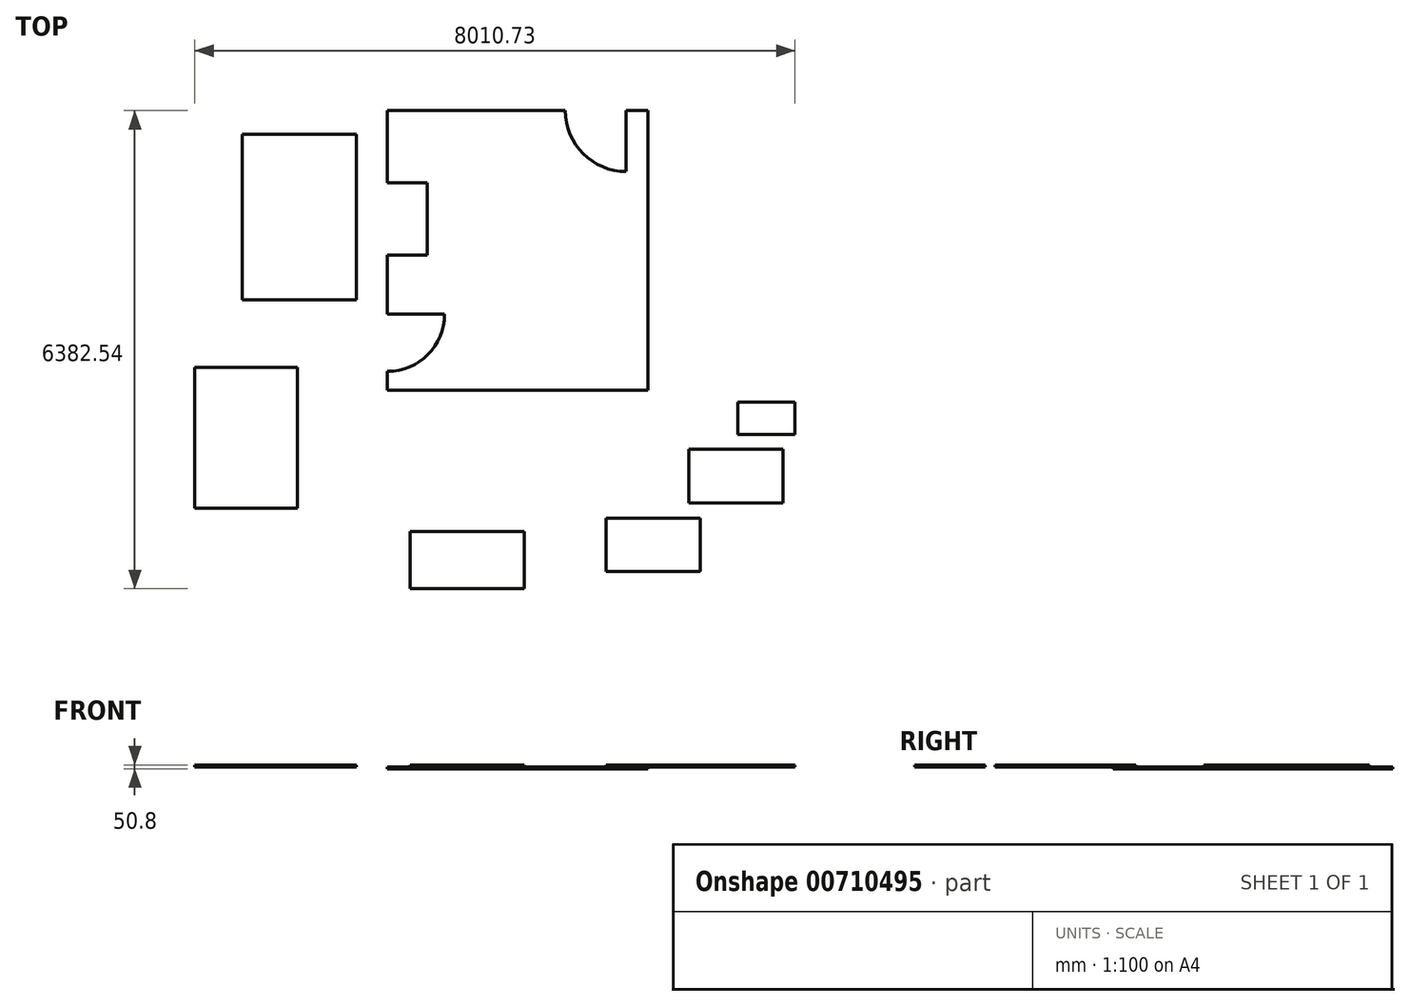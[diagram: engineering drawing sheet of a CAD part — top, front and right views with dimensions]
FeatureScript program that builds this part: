
annotation { "Feature Type Name" : "Feature", "Feature Type Description" : "" }
export const myFeature = defineFeature(function(context is Context, id is Id, definition is map)
    precondition{}
    {
        {
            var Q0;
            Q0=qCreatedBy(makeId("Top.planeOp"),FACE);
            var sketch = newSketch(context, id + "F0", { "sketchPlane" : qUnion([Q0])});
            skLineSegment(sketch, "E0", {"start": v(-1733.33, 2522.98) * mm, "end": v(641.57, 2522.98) * mm});
            skLineSegment(sketch, "E1", {"start": v(1746.47, 2522.98) * mm, "end": v(1746.47, -1210.82) * mm});
            skLineSegment(sketch, "E2", {"start": v(1746.47, -1210.82) * mm, "end": v(-1733.33, -1210.82) * mm});
            skLineSegment(sketch, "E3", {"start": v(-1733.33, -1210.82) * mm, "end": v(-1733.33, -956.82) * mm});
            skLineSegment(sketch, "E4", {"start": v(-1733.33, 592.58) * mm, "end": v(-1199.93, 592.58) * mm});
            skLineSegment(sketch, "E5", {"start": v(-1199.93, 592.58) * mm, "end": v(-1199.93, 1557.78) * mm});
            skLineSegment(sketch, "E6", {"start": v(-1199.93, 1557.78) * mm, "end": v(-1733.33, 1557.78) * mm});
            skLineSegment(sketch, "E7", {"start": v(-1733.33, 1557.78) * mm, "end": v(-1733.33, 2522.98) * mm});
            skArc(sketch, "E8", {"start": v(-1733.33, -956.82) * mm, "mid": v(-1194.52, -733.64) * mm, "end": v(-971.33, -194.82) * mm});
            skLineSegment(sketch, "E9", {"start": v(-1733.33, -194.82) * mm, "end": v(-971.33, -194.82) * mm});
            skLineSegment(sketch, "E10.trimOffspring", {"start": v(-1733.33, -194.82) * mm, "end": v(-1733.33, 592.58) * mm});
            skArc(sketch, "E11", {"start": v(641.57, 2522.98) * mm, "mid": v(879.63, 1948.24) * mm, "end": v(1454.37, 1710.18) * mm});
            skLineSegment(sketch, "E12", {"start": v(1454.37, 2522.98) * mm, "end": v(1454.37, 1710.18) * mm});
            skLineSegment(sketch, "E13.trimOffspring", {"start": v(1454.37, 2522.98) * mm, "end": v(1746.47, 2522.98) * mm});
            skSolve(sketch);
        }
        {
            var Q0;
            Q0 = qSketchRegion(id + "F0", true);
            extrude(context, id + "F1", {"entities" : qUnion([Q0]), "depth" : 25.4 * mm, "offsetDistance" : 25.4 * mm});
        }
        {
            var Q0;
            Q0=makeQuery(id+"F1.opExtrude","CAP_FACE",FACE,{"disambiguationData":[OSD([sQuery(id+"F0.wireOp",EDGE,"E0"),sQuery(id+"F0.wireOp",EDGE,"E1"),sQuery(id+"F0.wireOp",EDGE,"E2"),sQuery(id+"F0.wireOp",EDGE,"E3"),sQuery(id+"F0.wireOp",EDGE,"E4"),sQuery(id+"F0.wireOp",EDGE,"E5"),sQuery(id+"F0.wireOp",EDGE,"E6"),sQuery(id+"F0.wireOp",EDGE,"E7")])],"isStart":false});
            var sketch = newSketch(context, id + "F2", { "sketchPlane" : qUnion([Q0])});
            skLineSegment(sketch, "E14.bottom", {"start": v(-3670.25, 2209.8) * mm, "end": v(-2146.25, 2209.8) * mm});
            skLineSegment(sketch, "E14.top", {"start": v(-3670.25, 0) * mm, "end": v(-2146.25, 0) * mm});
            skLineSegment(sketch, "E14.left", {"start": v(-3670.25, 2209.8) * mm, "end": v(-3670.25, 0) * mm});
            skLineSegment(sketch, "E14.right", {"start": v(-2146.25, 2209.8) * mm, "end": v(-2146.25, 0) * mm});
            skSolve(sketch);
        }
        {
            var Q0;
            Q0=makeQuery(id+"F2.imprint","IMPRINT",FACE,{"disambiguationData":[TD([[makeQuery(id+"F2.imprint","IMPRINT",EDGE,{"derivedFrom":sQuery(id+"F2.wireOp",EDGE,"E14.bottom")}),-1.0]])]});
            extrude(context, id + "F3", {"entities" : qUnion([Q0]), "depth" : 25.4 * mm, "offsetDistance" : 25.4 * mm});
        }
        {
            var Q0;
            Q0=makeQuery(id+"F1.opExtrude","CAP_FACE",FACE,{"disambiguationData":[OSD([sQuery(id+"F0.wireOp",EDGE,"E0"),sQuery(id+"F0.wireOp",EDGE,"E1"),sQuery(id+"F0.wireOp",EDGE,"E2"),sQuery(id+"F0.wireOp",EDGE,"E3"),sQuery(id+"F0.wireOp",EDGE,"E4"),sQuery(id+"F0.wireOp",EDGE,"E5"),sQuery(id+"F0.wireOp",EDGE,"E6"),sQuery(id+"F0.wireOp",EDGE,"E7")])],"isStart":false});
            var sketch = newSketch(context, id + "F4", { "sketchPlane" : qUnion([Q0])});
            skLineSegment(sketch, "E15.bottom", {"start": v(-4305.32, -903.13) * mm, "end": v(-2933.72, -903.13) * mm});
            skLineSegment(sketch, "E15.top", {"start": v(-4305.32, -2782.73) * mm, "end": v(-2933.72, -2782.73) * mm});
            skLineSegment(sketch, "E15.left", {"start": v(-4305.32, -903.13) * mm, "end": v(-4305.32, -2782.73) * mm});
            skLineSegment(sketch, "E15.right", {"start": v(-2933.72, -903.13) * mm, "end": v(-2933.72, -2782.73) * mm});
            skSolve(sketch);
        }
        {
            var Q0;
            Q0=makeQuery(id+"F4.imprint","IMPRINT",FACE,{"disambiguationData":[TD([[makeQuery(id+"F4.imprint","IMPRINT",EDGE,{"derivedFrom":sQuery(id+"F4.wireOp",EDGE,"E15.bottom")}),-1.0]])]});
            extrude(context, id + "F5", {"entities" : qUnion([Q0]), "depth" : 25.4 * mm, "offsetDistance" : 25.4 * mm});
        }
        {
            var Q0;
            Q0=makeQuery(id+"F1.opExtrude","CAP_FACE",FACE,{"disambiguationData":[OSD([sQuery(id+"F0.wireOp",EDGE,"E0"),sQuery(id+"F0.wireOp",EDGE,"E1"),sQuery(id+"F0.wireOp",EDGE,"E2"),sQuery(id+"F0.wireOp",EDGE,"E3"),sQuery(id+"F0.wireOp",EDGE,"E4"),sQuery(id+"F0.wireOp",EDGE,"E5"),sQuery(id+"F0.wireOp",EDGE,"E6"),sQuery(id+"F0.wireOp",EDGE,"E7")])],"isStart":false});
            var sketch = newSketch(context, id + "F6", { "sketchPlane" : qUnion([Q0])});
            skLineSegment(sketch, "E16.bottom", {"start": v(-1434.19, -3097.56) * mm, "end": v(89.81, -3097.56) * mm});
            skLineSegment(sketch, "E16.top", {"start": v(-1434.19, -3859.56) * mm, "end": v(89.81, -3859.56) * mm});
            skLineSegment(sketch, "E16.left", {"start": v(-1434.19, -3097.56) * mm, "end": v(-1434.19, -3859.56) * mm});
            skLineSegment(sketch, "E16.right", {"start": v(89.81, -3097.56) * mm, "end": v(89.81, -3859.56) * mm});
            skSolve(sketch);
        }
        {
            var Q0;
            Q0=makeQuery(id+"F6.imprint","IMPRINT",FACE,{"disambiguationData":[TD([[makeQuery(id+"F6.imprint","IMPRINT",EDGE,{"derivedFrom":sQuery(id+"F6.wireOp",EDGE,"E16.bottom")}),-1.0]])]});
            extrude(context, id + "F7", {"entities" : qUnion([Q0]), "depth" : 25.4 * mm, "offsetDistance" : 25.4 * mm});
        }
        {
            var Q0;
            Q0=makeQuery(id+"F1.opExtrude","CAP_FACE",FACE,{"disambiguationData":[OSD([sQuery(id+"F0.wireOp",EDGE,"E0"),sQuery(id+"F0.wireOp",EDGE,"E1"),sQuery(id+"F0.wireOp",EDGE,"E2"),sQuery(id+"F0.wireOp",EDGE,"E3"),sQuery(id+"F0.wireOp",EDGE,"E4"),sQuery(id+"F0.wireOp",EDGE,"E5"),sQuery(id+"F0.wireOp",EDGE,"E6"),sQuery(id+"F0.wireOp",EDGE,"E7")])],"isStart":false});
            var sketch = newSketch(context, id + "F8", { "sketchPlane" : qUnion([Q0])});
            skLineSegment(sketch, "E17.bottom", {"start": v(1185.09, -2919.93) * mm, "end": v(2442.39, -2919.93) * mm});
            skLineSegment(sketch, "E17.top", {"start": v(1185.09, -3631.13) * mm, "end": v(2442.39, -3631.13) * mm});
            skLineSegment(sketch, "E17.left", {"start": v(1185.09, -2919.93) * mm, "end": v(1185.09, -3631.13) * mm});
            skLineSegment(sketch, "E17.right", {"start": v(2442.39, -2919.93) * mm, "end": v(2442.39, -3631.13) * mm});
            skSolve(sketch);
        }
        {
            var Q0;
            Q0 = qSketchRegion(id + "F8", true);
            extrude(context, id + "F9", {"entities" : qUnion([Q0]), "depth" : 25.4 * mm, "offsetDistance" : 25.4 * mm});
        }
        {
            var Q0;
            Q0=makeQuery(id+"F1.opExtrude","CAP_FACE",FACE,{"disambiguationData":[OSD([sQuery(id+"F0.wireOp",EDGE,"E0"),sQuery(id+"F0.wireOp",EDGE,"E1"),sQuery(id+"F0.wireOp",EDGE,"E2"),sQuery(id+"F0.wireOp",EDGE,"E3"),sQuery(id+"F0.wireOp",EDGE,"E4"),sQuery(id+"F0.wireOp",EDGE,"E5"),sQuery(id+"F0.wireOp",EDGE,"E6"),sQuery(id+"F0.wireOp",EDGE,"E7"),sQuery(id+"F0.wireOp",EDGE,"E8"),sQuery(id+"F0.wireOp",EDGE,"E9"),sQuery(id+"F0.wireOp",EDGE,"E10.trimOffspring"),sQuery(id+"F0.wireOp",EDGE,"E11"),sQuery(id+"F0.wireOp",EDGE,"E12"),sQuery(id+"F0.wireOp",EDGE,"E13.trimOffspring")])],"isStart":false});
            var sketch = newSketch(context, id + "F10", { "sketchPlane" : qUnion([Q0])});
            skLineSegment(sketch, "E18.bottom", {"start": v(2943.41, -1369.79) * mm, "end": v(3705.41, -1369.79) * mm});
            skLineSegment(sketch, "E18.top", {"start": v(2943.41, -1801.59) * mm, "end": v(3705.41, -1801.59) * mm});
            skLineSegment(sketch, "E18.left", {"start": v(2943.41, -1369.79) * mm, "end": v(2943.41, -1801.59) * mm});
            skLineSegment(sketch, "E18.right", {"start": v(3705.41, -1369.79) * mm, "end": v(3705.41, -1801.59) * mm});
            skSolve(sketch);
        }
        {
            var Q0;
            Q0=makeQuery(id+"F10.imprint","IMPRINT",FACE,{"disambiguationData":[TD([[makeQuery(id+"F10.imprint","IMPRINT",EDGE,{"derivedFrom":sQuery(id+"F10.wireOp",EDGE,"E18.bottom")}),-1.0]])]});
            extrude(context, id + "F11", {"entities" : qUnion([Q0]), "depth" : 25.4 * mm, "offsetDistance" : 25.4 * mm});
        }
        {
            var Q0;
            Q0=makeQuery(id+"F1.opExtrude","CAP_FACE",FACE,{"disambiguationData":[OSD([sQuery(id+"F0.wireOp",EDGE,"E0"),sQuery(id+"F0.wireOp",EDGE,"E1"),sQuery(id+"F0.wireOp",EDGE,"E2"),sQuery(id+"F0.wireOp",EDGE,"E3"),sQuery(id+"F0.wireOp",EDGE,"E4"),sQuery(id+"F0.wireOp",EDGE,"E5"),sQuery(id+"F0.wireOp",EDGE,"E6"),sQuery(id+"F0.wireOp",EDGE,"E7"),sQuery(id+"F0.wireOp",EDGE,"E8"),sQuery(id+"F0.wireOp",EDGE,"E9"),sQuery(id+"F0.wireOp",EDGE,"E10.trimOffspring"),sQuery(id+"F0.wireOp",EDGE,"E11"),sQuery(id+"F0.wireOp",EDGE,"E12"),sQuery(id+"F0.wireOp",EDGE,"E13.trimOffspring")])],"isStart":false});
            var sketch = newSketch(context, id + "F12", { "sketchPlane" : qUnion([Q0])});
            skLineSegment(sketch, "E19.bottom", {"start": v(2291.9, -1998.48) * mm, "end": v(3549.2, -1998.48) * mm});
            skLineSegment(sketch, "E19.top", {"start": v(2291.9, -2716.03) * mm, "end": v(3549.2, -2716.03) * mm});
            skLineSegment(sketch, "E19.left", {"start": v(2291.9, -1998.48) * mm, "end": v(2291.9, -2716.03) * mm});
            skLineSegment(sketch, "E19.right", {"start": v(3549.2, -1998.48) * mm, "end": v(3549.2, -2716.03) * mm});
            skSolve(sketch);
        }
        {
            var Q0;
            Q0=makeQuery(id+"F12.imprint","IMPRINT",FACE,{"disambiguationData":[TD([[makeQuery(id+"F12.imprint","IMPRINT",EDGE,{"derivedFrom":sQuery(id+"F12.wireOp",EDGE,"E19.bottom")}),-1.0]])]});
            extrude(context, id + "F13", {"entities" : qUnion([Q0]), "depth" : 25.4 * mm, "offsetDistance" : 25.4 * mm});
        }
    });
